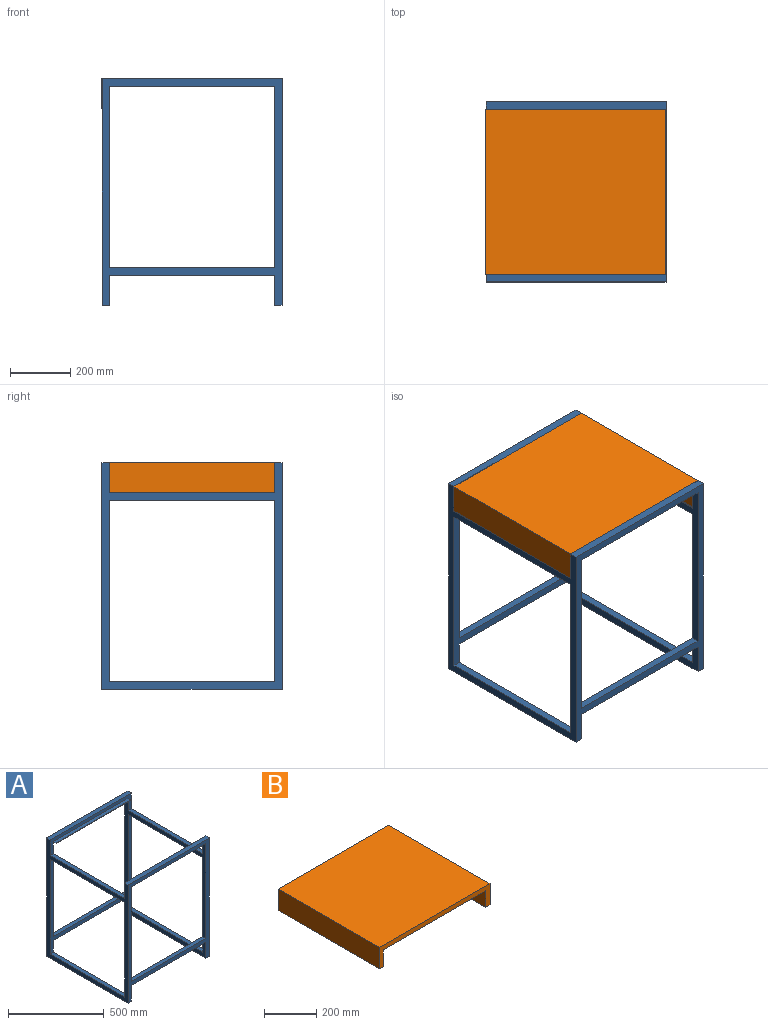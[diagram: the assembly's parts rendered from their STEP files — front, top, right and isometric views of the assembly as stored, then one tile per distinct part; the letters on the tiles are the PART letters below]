
ASSEMBLY  parts=2 mates=1
PART A: 36 faces, bbox 600x600x755 mm
  f0: plane 600x100mm, normal (0,-1,0), area 17100mm2, adj f1,f2,f3,f14,f15,f24,f27,f28
  f1: plane 600x25mm, normal (0,0,1), area 15000mm2, adj f0,f2,f3,f7
  f2: plane 755x600mm, normal (1,0,0), area 65250mm2, adj f0,f1,f6,f7,f8,f9,f10,f11
  f3: plane 755x600mm, normal (-1,0,0), area 65250mm2, adj f0,f1,f7,f8,f9,f10,f11,f12
  f4: plane 600x100mm, normal (-1,0,0), area 18750mm2, adj f6,f7,f8,f9,f11,f16,f19,f26
  f5: plane 600x100mm, normal (1,0,0), area 18750mm2, adj f7,f8,f9,f11,f13,f16,f19,f22
  f6: plane 600x25mm, normal (0,0,-1), area 15000mm2, adj f2,f4,f7,f8
  f7: plane 755x600mm, normal (0,1,0), area 65250mm2, adj f1,f2,f3,f4,f5,f6,f13,f14
  f8: plane 755x600mm, normal (0,-1,0), area 65250mm2, adj f2,f3,f4,f5,f6,f12,f13,f14
  f9: plane 605x600mm, normal (0,-1,0), area 44000mm2, adj f2,f3,f4,f5,f14,f15,f19,f21
  f10: plane 600x100mm, normal (0,1,0), area 17100mm2, adj f2,f3,f12,f14,f15,f24,f27,f32
  f11: plane 605x600mm, normal (0,1,0), area 44000mm2, adj f2,f3,f4,f5,f14,f15,f16,f18
  f12: plane 600x25mm, normal (0,0,1), area 15000mm2, adj f2,f3,f8,f10
  f13: plane 600x25mm, normal (0,0,-1), area 15000mm2, adj f3,f5,f7,f8
  f14: plane 605x600mm, normal (-1,0,0), area 44000mm2, adj f0,f7,f8,f9,f10,f11,f17,f18
  f15: plane 605x600mm, normal (1,0,0), area 44000mm2, adj f0,f7,f8,f9,f10,f11,f17,f18
  f16: plane 550x25mm, normal (0,0,-1), area 13750mm2, adj f4,f5,f8,f11
  f17: plane 550x45mm, normal (0,0,-1), area 24750mm2, adj f8,f14,f15,f32,f33,f34
  f18: plane 550x25mm, normal (0,0,1), area 13750mm2, adj f8,f11,f14,f15
  f19: plane 550x25mm, normal (0,0,-1), area 13750mm2, adj f4,f5,f7,f9
  f20: plane 550x45mm, normal (0,0,-1), area 24750mm2, adj f7,f14,f15,f28,f29,f30
  f21: plane 550x25mm, normal (0,0,1), area 13750mm2, adj f7,f9,f14,f15
  f22: plane 550x25mm, normal (0,0,1), area 13750mm2, adj f3,f5,f9,f11
  f23: plane 550x25mm, normal (0,0,-1), area 13750mm2, adj f3,f9,f11,f15
  f24: plane 550x25mm, normal (0,0,1), area 13750mm2, adj f0,f3,f10,f15
  f25: plane 550x25mm, normal (0,0,-1), area 13750mm2, adj f2,f9,f11,f14
  f26: plane 550x25mm, normal (0,0,1), area 13750mm2, adj f2,f4,f9,f11
  f27: plane 550x25mm, normal (0,0,1), area 13750mm2, adj f0,f2,f10,f14
  f28: plane 20x3mm, normal (-1,0,0), area 60mm2, adj f0,f20,f30,f31
  f29: plane 20x3mm, normal (1,0,0), area 60mm2, adj f0,f20,f30,f31
  f30: plane 550x3mm, normal (0,-1,0), area 1650mm2, adj f20,f28,f29,f31
  f31: plane 550x20mm, normal (0,0,1), area 11000mm2, adj f0,f28,f29,f30
  f32: plane 20x3mm, normal (-1,0,0), area 60mm2, adj f10,f17,f33,f35
  f33: plane 550x3mm, normal (0,1,0), area 1650mm2, adj f17,f32,f34,f35
  f34: plane 20x3mm, normal (1,0,0), area 60mm2, adj f10,f17,f33,f35
  f35: plane 550x20mm, normal (0,0,1), area 11000mm2, adj f10,f32,f33,f34
PART B: 10 faces, bbox 600x550x100 mm
  f0: plane 556x550mm, normal (0,0,-1), area 305800mm2, adj f2,f4,f6,f8
  f1: plane 550x100mm, normal (1,0,0), area 55000mm2, adj f2,f4,f5,f7
  f2: plane 600x100mm, normal (0,1,0), area 16632mm2, adj f0,f1,f3,f5,f6,f7,f8,f9
  f3: plane 550x100mm, normal (-1,0,0), area 55000mm2, adj f2,f4,f5,f9
  f4: plane 600x100mm, normal (0,-1,0), area 16632mm2, adj f0,f1,f3,f5,f6,f7,f8,f9
  f5: plane 600x550mm, normal (0,0,1), area 330000mm2, adj f1,f2,f3,f4
  f6: plane 550x78mm, normal (-1,0,0), area 42900mm2, adj f0,f2,f4,f7
  f7: plane 550x22mm, normal (0,0,-1), area 12100mm2, adj f1,f2,f4,f6
  f8: plane 550x78mm, normal (1,0,0), area 42900mm2, adj f0,f2,f4,f9
  f9: plane 550x22mm, normal (0,0,-1), area 12100mm2, adj f2,f3,f4,f8
PLACE A t=(-426.03,-120.95,255.37)mm fixed
PLACE B t=(-426.22,-120.74,1010.37)mm
MATE planar B.f7 <-> A.f27  axis (0,0,-1) through (-137.22,-120.74,910.37)mm
